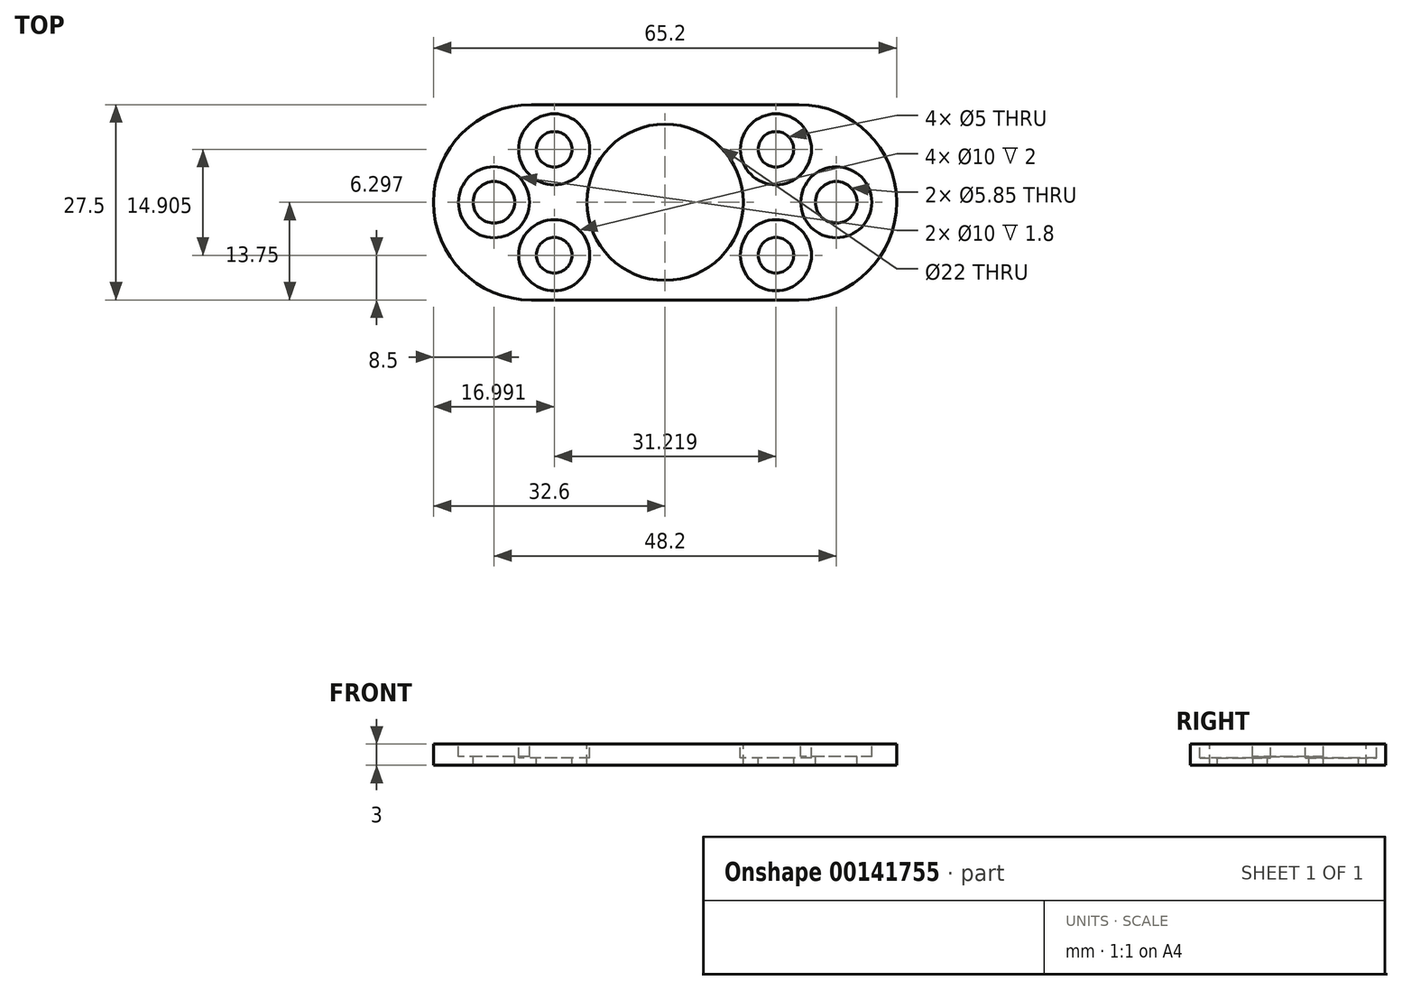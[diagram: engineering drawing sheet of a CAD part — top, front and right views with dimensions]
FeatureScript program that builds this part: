
annotation { "Feature Type Name" : "Feature", "Feature Type Description" : "" }
export const myFeature = defineFeature(function(context is Context, id is Id, definition is map)
    precondition{}
    {
        {
            var Q0;
            Q0=qCreatedBy(makeId("Top.planeOp"),FACE);
            var sketch = newSketch(context, id + "F0", { "sketchPlane" : qUnion([Q0])});
            skArc(sketch, "E0", {"start": v(-18.85, 13.75) * mm, "mid": v(-32.6, 0) * mm, "end": v(-18.85, -13.75) * mm});
            skArc(sketch, "E1.MirrorC", {"start": v(18.85, 13.75) * mm, "mid": v(32.6, 0) * mm, "end": v(18.85, -13.75) * mm});
            skLineSegment(sketch, "E2", {"start": v(-18.85, 13.75) * mm, "end": v(18.85, 13.75) * mm});
            skLineSegment(sketch, "E3", {"start": v(-18.85, -13.75) * mm, "end": v(18.85, -13.75) * mm});
            skCircle(sketch, "E4", {"center": v(-24.1, 0) * mm, "radius": 2.25 * mm, "construction": true});
            skCircle(sketch, "E5", {"center": v(0, 0) * mm, "radius": 11 * mm});
            skCircle(sketch, "E6", {"center": v(18.9, 0) * mm, "radius": 2.22 * mm, "construction": true});
            skCircle(sketch, "E7.MirrorC", {"center": v(24.1, 0) * mm, "radius": 2.25 * mm, "construction": true});
            skCircle(sketch, "E8", {"center": v(-15.6, 7.45) * mm, "radius": 6.3 * mm, "construction": true});
            skCircle(sketch, "E9", {"center": v(-24.1, 0) * mm, "radius": 5 * mm, "construction": true});
            skCircle(sketch, "E10.MirrorC", {"center": v(15.6, 7.45) * mm, "radius": 6.3 * mm, "construction": true});
            skCircle(sketch, "E11.MirrorC", {"center": v(-15.6, -7.45) * mm, "radius": 6.3 * mm, "construction": true});
            skCircle(sketch, "E12.MirrorC", {"center": v(15.6, -7.45) * mm, "radius": 6.3 * mm, "construction": true});
            skSolve(sketch);
        }
        {
            var Q0;
            Q0=makeQuery(id+"F0.imprint","IMPRINT",FACE,{"disambiguationData":[TD([[makeQuery(id+"F0.imprint","IMPRINT",EDGE,{"derivedFrom":sQuery(id+"F0.wireOp",EDGE,"E0")}),1.0]])]});
            extrude(context, id + "F1", {"entities" : qUnion([Q0]), "oppositeDirection" : true, "depth" : 3 * mm});
        }
        {
            var Q0;
            Q0=sQuery(id+"F0.wireOp",VERTEX,"b00cd72d-f22d-49a0-99af-2aa40ff85d85");
            var Q1;
            Q1=sQuery(id+"F0.wireOp",VERTEX,"E7.MirrorC.center");
            var Q2;
            Q2=sQuery(id+"F0.wireOp",VERTEX,"E4.center");
            var Q3;
            Q3=makeQuery(id+"F1.opExtrude","SWEPT_BODY",BODY,{"disambiguationData":[OSD([sQuery(id+"F0.wireOp",EDGE,"PKiLa4uU-TRW0-01Cl-qbqh-4NOdcOxrXYFE"),sQuery(id+"F0.wireOp",EDGE,"z3TDTkZm-GXDn-Mj3t-KOb2-9DUPlqvKWxhO"),sQuery(id+"F0.wireOp",EDGE,"OMRfVay1-SzMp-rEHD-UDvA-hLa8dMO30ZC0"),sQuery(id+"F0.wireOp",EDGE,"455976fe-0dce-462c-b297-5d2e9d4c9dec.trimOffspring"),sQuery(id+"F0.wireOp",EDGE,"E5")])]});
            hole(context, id + "F2", {"style" : HoleStyle.C_BORE, "endStyle" : HoleEndStyle.THROUGH, "holeDiameter" : 5.85 * mm, "cBoreDiameter" : 10 * mm, "cBoreDepth" : (1.2 + 0.6) * mm, "locations" : qUnion([Q0, Q1, Q2]), "scope" : qUnion([Q3]), "tappedDepth" : 12 * mm, "tapClearance" : 3});
        }
        {
            var Q0;
            Q0=sQuery(id+"F0.wireOp",VERTEX,"E8.center");
            var Q1;
            Q1=sQuery(id+"F0.wireOp",VERTEX,"E11.MirrorC.center");
            var Q2;
            Q2=sQuery(id+"F0.wireOp",VERTEX,"E12.MirrorC.center");
            var Q3;
            Q3=sQuery(id+"F0.wireOp",VERTEX,"E10.MirrorC.center");
            var Q4;
            Q4=makeQuery(id+"F1.opExtrude","SWEPT_BODY",BODY,{"disambiguationData":[OSD([sQuery(id+"F0.wireOp",EDGE,"E0"),sQuery(id+"F0.wireOp",EDGE,"E1.MirrorC"),sQuery(id+"F0.wireOp",EDGE,"E2"),sQuery(id+"F0.wireOp",EDGE,"E3"),sQuery(id+"F0.wireOp",EDGE,"E5")])]});
            hole(context, id + "F3", {"style" : HoleStyle.C_BORE, "endStyle" : HoleEndStyle.THROUGH, "holeDiameter" : 5 * mm, "cBoreDiameter" : 10 * mm, "cBoreDepth" : 2 * mm, "tappedDepth" : 12 * mm, "tapClearance" : 3, "locations" : qUnion([Q0, Q1, Q2, Q3]), "scope" : qUnion([Q4])});
        }
    });
